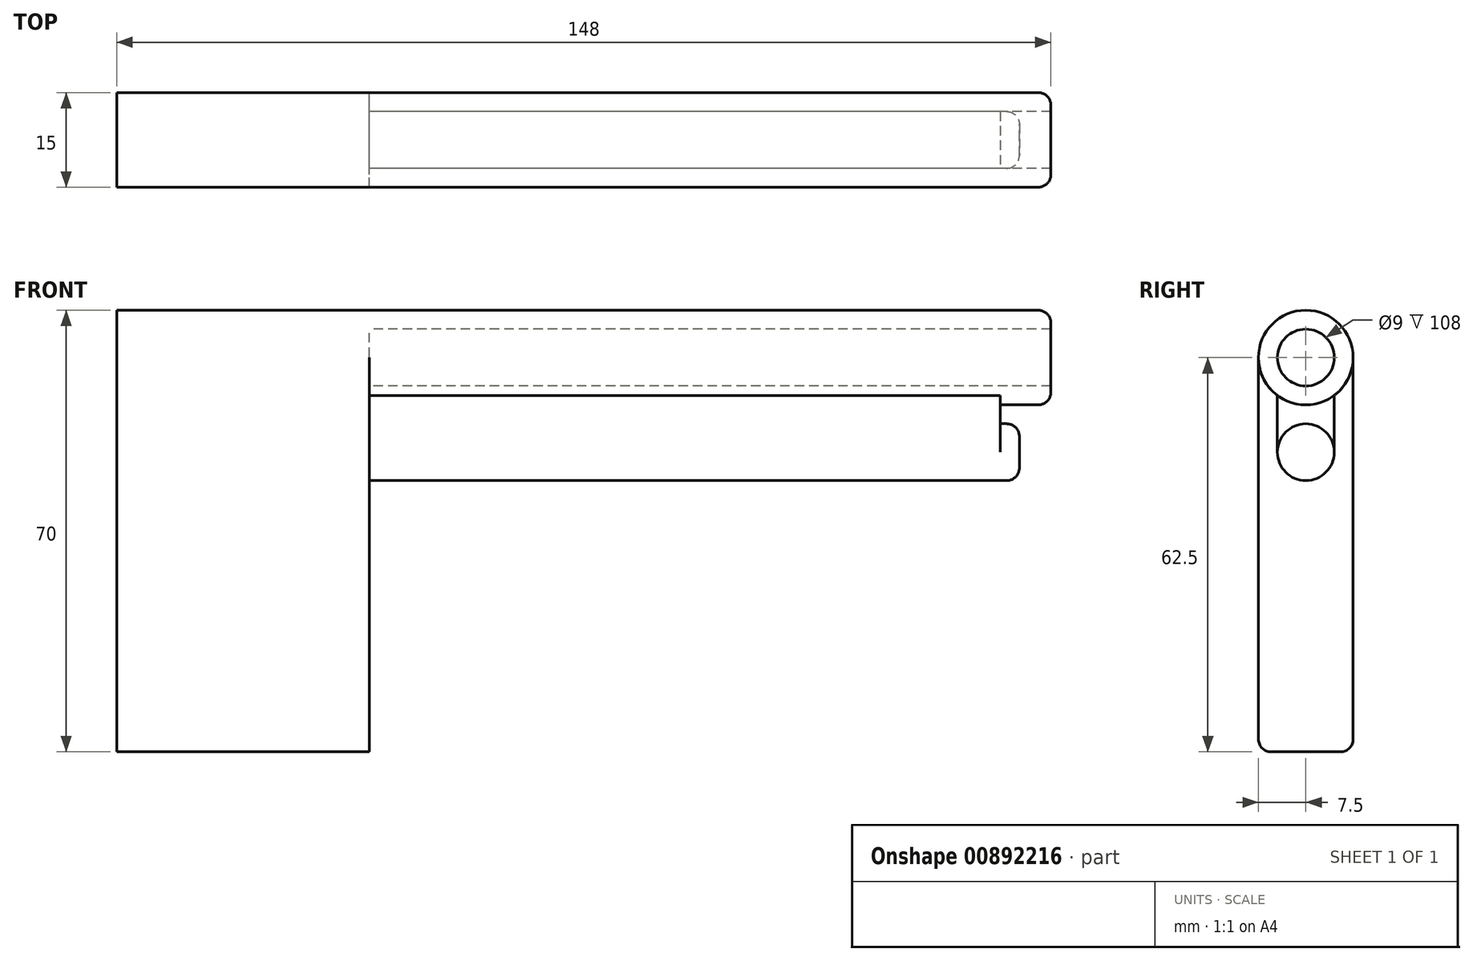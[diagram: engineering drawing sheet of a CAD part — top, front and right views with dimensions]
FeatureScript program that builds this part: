
annotation { "Feature Type Name" : "Feature", "Feature Type Description" : "" }
export const myFeature = defineFeature(function(context is Context, id is Id, definition is map)
    precondition{}
    {
        {
            var Q0;
            Q0=qCreatedBy(makeId("Right.planeOp"),FACE);
            var sketch = newSketch(context, id + "F0", { "sketchPlane" : qUnion([Q0])});
            skCircle(sketch, "E0", {"center": v(0, 0) * mm, "radius": 4.5 * mm});
            skCircle(sketch, "E1", {"center": v(0, 0) * mm, "radius": 7.5 * mm});
            skCircle(sketch, "E2", {"center": v(0, -15) * mm, "radius": 4.5 * mm});
            skLineSegment(sketch, "E3", {"start": v(4.5, -15) * mm, "end": v(4.5, -6) * mm});
            skLineSegment(sketch, "E4", {"start": v(-4.5, -15) * mm, "end": v(-4.5, -6) * mm});
            skSolve(sketch);
        }
        {
            var Q0;
            {var subQ0=sQuery(id+"F0.wireOp",EDGE,"E2");var subQ1=makeQuery(id+"F0.imprint","INTERSECT",VERTEX,{"derivedFrom":[subQ0,sQuery(id+"F0.wireOp",EDGE,"E3")]});Q0=makeQuery(id+"F0.imprint","IMPRINT",FACE,{"disambiguationData":[TD([[makeQuery(id+"F0.imprint","IMPRINT",EDGE,{"disambiguationData":[TD([[subQ1,-1.0]])],"derivedFrom":subQ0}),1.0]])]});}
            extrude(context, id + "F1", {"entities" : qUnion([Q0]), "depth" : 103 * mm, "offsetDistance" : 25 * mm});
        }
        {
            var Q0;
            {var subQ0=sQuery(id+"F0.wireOp",EDGE,"E3");Q0=makeQuery(id+"F0.imprint","IMPRINT",FACE,{"disambiguationData":[TD([[makeQuery(id+"F0.imprint","IMPRINT",EDGE,{"derivedFrom":subQ0}),1.0]])]});}
            extrude(context, id + "F2", {"entities" : qUnion([Q0]), "operationType" : NewBodyOperationType.ADD, "depth" : 100 * mm, "offsetDistance" : 25 * mm});
        }
        {
            var Q0;
            Q0=makeQuery(id+"F0.imprint","IMPRINT",FACE,{"disambiguationData":[TD([[makeQuery(id+"F0.imprint","IMPRINT",EDGE,{"derivedFrom":sQuery(id+"F0.wireOp",EDGE,"E0")}),-1.0]])]});
            extrude(context, id + "F3", {"entities" : qUnion([Q0]), "operationType" : NewBodyOperationType.ADD, "depth" : 108 * mm, "offsetDistance" : 25 * mm});
        }
        {
            var Q0;
            Q0=makeQuery(id+"F3.opExtrude","CAP_EDGE",EDGE,{"disambiguationData":[OSD([sQuery(id+"F0.wireOp",EDGE,"E1")])],"isStart":false});
            fillet(context, id + "F4", {"entities" : qUnion([Q0]), "radius" : 2 * mm, "tangentPropagation" : true, "allowEdgeOverflow" : false});
        }
        {
            var Q0;
            Q0=makeQuery(id+"F1.opExtrude","CAP_EDGE",EDGE,{"disambiguationData":[OSD([sQuery(id+"F0.wireOp",EDGE,"E2")])],"isStart":false});
            fillet(context, id + "F5", {"entities" : qUnion([Q0]), "radius" : 2 * mm, "tangentPropagation" : true, "allowEdgeOverflow" : false});
        }
        {
            var Q0;
            Q0=qCreatedBy(makeId("Right.planeOp"),FACE);
            var sketch = newSketch(context, id + "F6", { "sketchPlane" : qUnion([Q0])});
            skLineSegment(sketch, "E5.bottom", {"start": v(0, 7.5) * mm, "end": v(0, 7.5) * mm});
            skLineSegment(sketch, "E5.top", {"start": v(-5.5, -62.5) * mm, "end": v(5.5, -62.5) * mm});
            skLineSegment(sketch, "E5.left", {"start": v(-7.5, 0) * mm, "end": v(-7.5, -60.5) * mm});
            skLineSegment(sketch, "E5.right", {"start": v(7.5, 0) * mm, "end": v(7.5, -60.5) * mm});
            skPoint(sketch, "E6.visualSharp", {"position": v(-7.5, 7.5) * mm});
            skArc(sketch, "E6.filletArc", {"start": v(0, 7.5) * mm, "mid": v(-5.3, 5.3) * mm, "end": v(-7.5, 0) * mm});
            skPoint(sketch, "E7.visualSharp", {"position": v(7.5, 7.5) * mm});
            skArc(sketch, "E7.filletArc", {"start": v(7.5, 0) * mm, "mid": v(5.3, 5.3) * mm, "end": v(0, 7.5) * mm});
            skPoint(sketch, "E8.visualSharp", {"position": v(-7.5, -62.5) * mm});
            skArc(sketch, "E8.filletArc", {"start": v(-7.5, -60.5) * mm, "mid": v(-6.91, -61.91) * mm, "end": v(-5.5, -62.5) * mm});
            skPoint(sketch, "E9.visualSharp", {"position": v(7.5, -62.5) * mm});
            skArc(sketch, "E9.filletArc", {"start": v(5.5, -62.5) * mm, "mid": v(6.91, -61.91) * mm, "end": v(7.5, -60.5) * mm});
            skSolve(sketch);
        }
        {
            var Q0;
            Q0=makeQuery(id+"F6.imprint","IMPRINT",FACE,{"disambiguationData":[TD([[makeQuery(id+"F6.imprint","IMPRINT",EDGE,{"derivedFrom":sQuery(id+"F6.wireOp",EDGE,"E5.top")}),1.0]])]});
            extrude(context, id + "F7", {"entities" : qUnion([Q0]), "operationType" : NewBodyOperationType.ADD, "oppositeDirection" : true, "depth" : 40 * mm, "offsetDistance" : 25 * mm});
        }
    });
